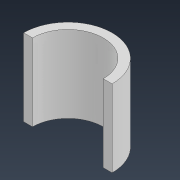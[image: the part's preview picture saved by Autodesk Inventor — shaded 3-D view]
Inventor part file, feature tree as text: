
AUTODESK INVENTOR PART (.ipt)
format: ipt  version: 2022 (Build 260153000, 153)  size: 89,088 bytes
history: native  units: mm
features: extrude x1, sketch x1
ambient origin geometry x8: Origin, YZ Plane, XZ Plane, XY Plane, X Axis, Y Axis, Z Axis, Center Point
bodies: Solid1 (feature_tree)
feature tree (2):
  extrude  "Extrusion1"  Depth=21.76mm
  sketch  "Sketch1"  dims[d0=20.0mm d1=25.0mm d2=21.76mm d3=0.0mm]
